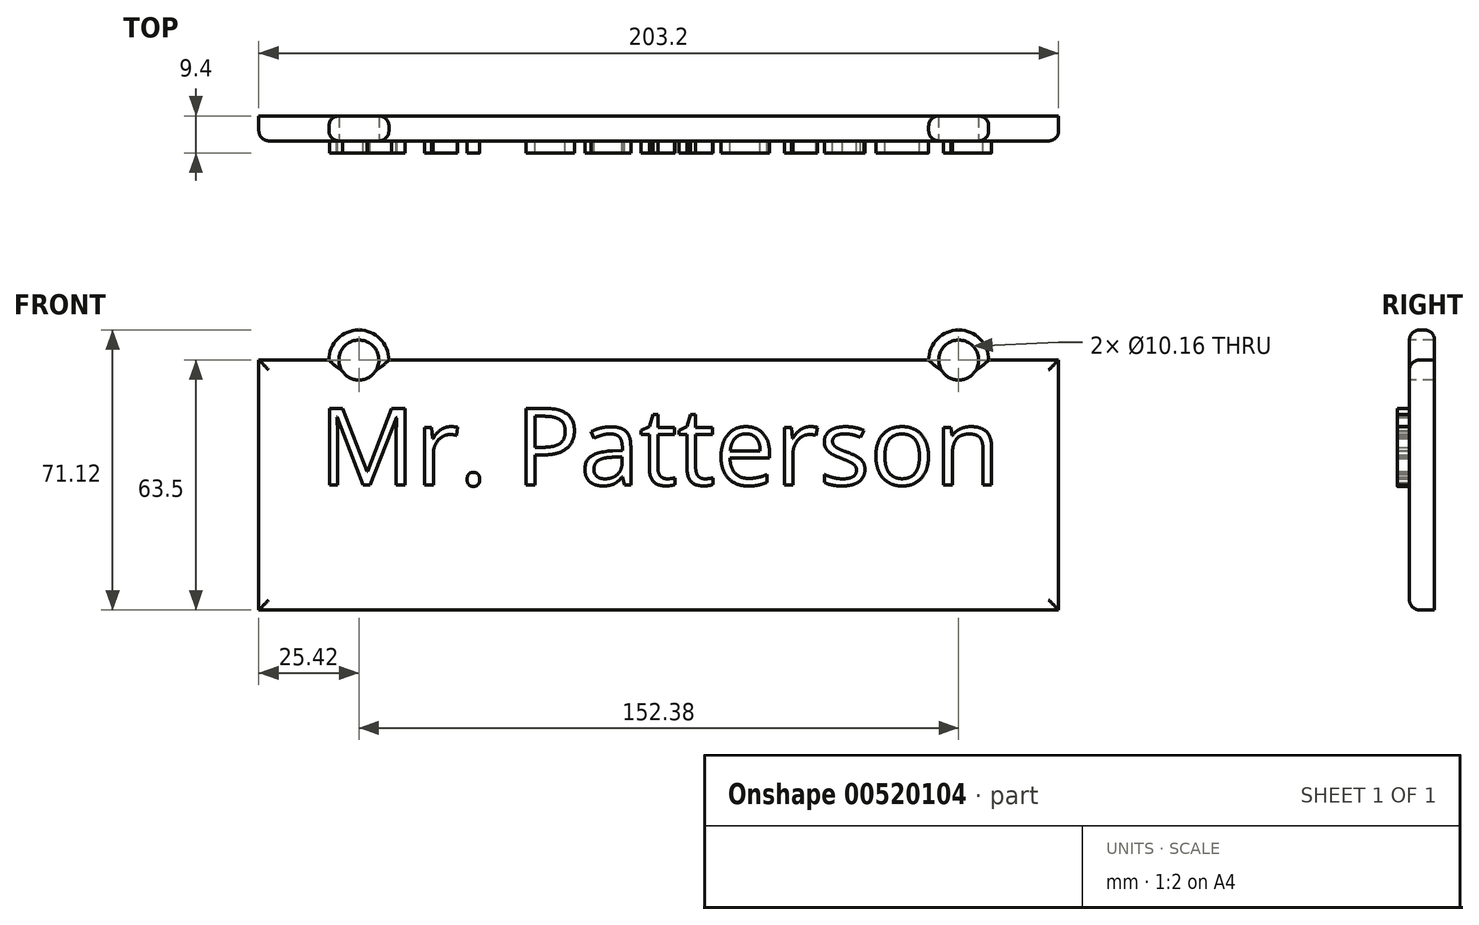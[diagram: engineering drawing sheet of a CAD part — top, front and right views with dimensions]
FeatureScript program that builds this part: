
annotation { "Feature Type Name" : "Feature", "Feature Type Description" : "" }
export const myFeature = defineFeature(function(context is Context, id is Id, definition is map)
    precondition{}
    {
        {
            var Q0;
            Q0=qCreatedBy(makeId("Front.planeOp"),FACE);
            var sketch = newSketch(context, id + "F0", { "sketchPlane" : qUnion([Q0])});
            skLineSegment(sketch, "E0.bottom", {"start": v(101.6, 31.75) * mm, "end": v(-101.6, 31.75) * mm});
            skLineSegment(sketch, "E0.top", {"start": v(101.6, -31.75) * mm, "end": v(-101.6, -31.75) * mm});
            skLineSegment(sketch, "E0.left", {"start": v(101.6, 31.75) * mm, "end": v(101.6, -31.75) * mm});
            skLineSegment(sketch, "E0.right", {"start": v(-101.6, 31.75) * mm, "end": v(-101.6, -31.75) * mm});
            skPoint(sketch, "E0.middle", {"position": v(0, 0) * mm});
            skSolve(sketch);
        }
        {
            var Q0;
            Q0=makeQuery(id+"F0.imprint","IMPRINT",FACE,{"disambiguationData":[TD([[makeQuery(id+"F0.imprint","IMPRINT",EDGE,{"derivedFrom":sQuery(id+"F0.wireOp",EDGE,"E0.bottom")}),1.0]])]});
            extrude(context, id + "F1", {"entities" : qUnion([Q0]), "depth" : 6.35 * mm, "offsetDistance" : 25.4 * mm});
        }
        {
            var Q0;
            Q0=makeQuery(id+"F1.opExtrude","CAP_FACE",FACE,{"disambiguationData":[OSD([sQuery(id+"F0.wireOp",EDGE,"E0.bottom"),sQuery(id+"F0.wireOp",EDGE,"E0.top"),sQuery(id+"F0.wireOp",EDGE,"E0.left"),sQuery(id+"F0.wireOp",EDGE,"E0.right")])],"isStart":false});
            var sketch = newSketch(context, id + "F2", { "sketchPlane" : qUnion([Q0])});
            skCircle(sketch, "E1", {"center": v(-76.18, 31.75) * mm, "radius": 7.62 * mm});
            skCircle(sketch, "E2", {"center": v(76.2, 31.75) * mm, "radius": 7.62 * mm});
            skSolve(sketch);
        }
        {
            var Q0;
            {var subQ0=sQuery(id+"F2.wireOp",EDGE,"E1");var subQ1=makeQuery(id+"F1.opExtrude","CAP_EDGE",EDGE,{"disambiguationData":[OSD([sQuery(id+"F0.wireOp",EDGE,"E0.bottom")])],"isStart":false});var subQ2=makeQuery(id+"F2.imprint","INTERSECT",VERTEX,{"disambiguationData":[OD(0.0)],"derivedFrom":[subQ1,subQ0]});Q0=makeQuery(id+"F2.imprint","IMPRINT",FACE,{"disambiguationData":[TD([[makeQuery(id+"F2.imprint","IMPRINT",EDGE,{"disambiguationData":[TD([[subQ2,1.0]])],"derivedFrom":subQ0}),1.0]])]});}
            var Q1;
            {var subQ0=sQuery(id+"F2.wireOp",EDGE,"E2");var subQ1=makeQuery(id+"F1.opExtrude","CAP_EDGE",EDGE,{"disambiguationData":[OSD([sQuery(id+"F0.wireOp",EDGE,"E0.bottom")])],"isStart":false});var subQ2=makeQuery(id+"F2.imprint","INTERSECT",VERTEX,{"disambiguationData":[OD(0.0)],"derivedFrom":[subQ1,subQ0]});Q1=makeQuery(id+"F2.imprint","IMPRINT",FACE,{"disambiguationData":[TD([[makeQuery(id+"F2.imprint","IMPRINT",EDGE,{"disambiguationData":[TD([[subQ2,-1.0]])],"derivedFrom":subQ0}),1.0]])]});}
            extrude(context, id + "F3", {"entities" : qUnion([Q0, Q1]), "operationType" : NewBodyOperationType.ADD, "depth" : -6.35 * mm, "offsetDistance" : 25.4 * mm});
        }
        {
            var Q0;
            {var subQ0=sQuery(id+"F0.wireOp",EDGE,"E0.bottom");Q0=makeQuery(id+"F3.boolean.opBoolean","MERGE",FACE,{"derivedFrom":[makeQuery(id+"F1.opExtrude","CAP_FACE",FACE,{"disambiguationData":[OSD([subQ0,sQuery(id+"F0.wireOp",EDGE,"E0.top"),sQuery(id+"F0.wireOp",EDGE,"E0.left"),sQuery(id+"F0.wireOp",EDGE,"E0.right")])],"isStart":false}),makeQuery(id+"F3.opExtrude","CAP_FACE",FACE,{"disambiguationData":[OSD([subQ0,sQuery(id+"F2.wireOp",EDGE,"E1")])],"isStart":true}),makeQuery(id+"F3.opExtrude","CAP_FACE",FACE,{"disambiguationData":[OSD([subQ0,sQuery(id+"F2.wireOp",EDGE,"E2")])],"isStart":true})]});}
            var sketch = newSketch(context, id + "F4", { "sketchPlane" : qUnion([Q0])});
            skCircle(sketch, "E3", {"center": v(-76.18, 31.75) * mm, "radius": 5.08 * mm});
            skCircle(sketch, "E4", {"center": v(76.2, 31.75) * mm, "radius": 5.08 * mm});
            skSolve(sketch);
        }
        {
            var Q0;
            Q0=makeQuery(id+"F4.imprint","IMPRINT",FACE,{"disambiguationData":[TD([[makeQuery(id+"F4.imprint","IMPRINT",EDGE,{"derivedFrom":sQuery(id+"F4.wireOp",EDGE,"E3")}),1.0]])]});
            var Q1;
            Q1=makeQuery(id+"F4.imprint","IMPRINT",FACE,{"disambiguationData":[TD([[makeQuery(id+"F4.imprint","IMPRINT",EDGE,{"derivedFrom":sQuery(id+"F4.wireOp",EDGE,"E4")}),1.0]])]});
            extrude(context, id + "F5", {"entities" : qUnion([Q0, Q1]), "operationType" : NewBodyOperationType.REMOVE, "oppositeDirection" : true, "depth" : 6.35 * mm, "offsetDistance" : 25.4 * mm});
        }
        {
            var Q0;
            Q0=makeQuery(id+"F1.opExtrude","CAP_EDGE",EDGE,{"disambiguationData":[OSD([sQuery(id+"F0.wireOp",EDGE,"E0.top")])],"isStart":false});
            var Q1;
            Q1=makeQuery(id+"F1.opExtrude","CAP_EDGE",EDGE,{"disambiguationData":[OSD([sQuery(id+"F0.wireOp",EDGE,"E0.right")])],"isStart":false});
            var Q2;
            {var subQ0=sQuery(id+"F2.wireOp",EDGE,"E1");var subQ1=sQuery(id+"F0.wireOp",EDGE,"E0.right");var subQ2=sQuery(id+"F0.wireOp",EDGE,"E0.bottom");Q2=makeQuery(id+"F3.boolean.opBoolean","SPLIT",EDGE,{"disambiguationData":[TD([makeQuery(id+"F1.opExtrude","SWEPT_FACE",FACE,{"disambiguationData":[OSD([subQ2])]}),makeQuery(id+"F1.opExtrude","CAP_FACE",FACE,{"disambiguationData":[OSD([subQ2,sQuery(id+"F0.wireOp",EDGE,"E0.top"),sQuery(id+"F0.wireOp",EDGE,"E0.left"),subQ1])],"isStart":false}),makeQuery(id+"F1.opExtrude","SWEPT_FACE",FACE,{"disambiguationData":[OSD([subQ1])]}),makeQuery(id+"F3.opExtrude","SWEPT_FACE",FACE,{"disambiguationData":[OSD([subQ0])]}),makeQuery(id+"F3.opExtrude","CAP_FACE",FACE,{"disambiguationData":[OSD([subQ2,subQ0])],"isStart":true}),makeQuery(id+"F3.opExtrude","CAP_FACE",FACE,{"disambiguationData":[OSD([subQ2,sQuery(id+"F2.wireOp",EDGE,"E2")])],"isStart":true})])],"derivedFrom":makeQuery(id+"F1.opExtrude","CAP_EDGE",EDGE,{"disambiguationData":[OSD([subQ2])],"isStart":false})});}
            var Q3;
            Q3=makeQuery(id+"F3.opExtrude","CAP_EDGE",EDGE,{"disambiguationData":[OSD([sQuery(id+"F2.wireOp",EDGE,"E1")])],"isStart":true});
            var Q4;
            {var subQ0=sQuery(id+"F2.wireOp",EDGE,"E1");var subQ1=sQuery(id+"F0.wireOp",EDGE,"E0.bottom");var subQ2=sQuery(id+"F2.wireOp",EDGE,"E2");Q4=makeQuery(id+"F3.boolean.opBoolean","SPLIT",EDGE,{"disambiguationData":[TD([makeQuery(id+"F1.opExtrude","SWEPT_FACE",FACE,{"disambiguationData":[OSD([subQ1])]}),makeQuery(id+"F1.opExtrude","CAP_FACE",FACE,{"disambiguationData":[OSD([subQ1,sQuery(id+"F0.wireOp",EDGE,"E0.top"),sQuery(id+"F0.wireOp",EDGE,"E0.left"),sQuery(id+"F0.wireOp",EDGE,"E0.right")])],"isStart":false}),makeQuery(id+"F3.opExtrude","SWEPT_FACE",FACE,{"disambiguationData":[OSD([subQ0])]}),makeQuery(id+"F3.opExtrude","CAP_FACE",FACE,{"disambiguationData":[OSD([subQ1,subQ0])],"isStart":true}),makeQuery(id+"F3.opExtrude","SWEPT_FACE",FACE,{"disambiguationData":[OSD([subQ2])]}),makeQuery(id+"F3.opExtrude","CAP_FACE",FACE,{"disambiguationData":[OSD([subQ1,subQ2])],"isStart":true})])],"derivedFrom":makeQuery(id+"F1.opExtrude","CAP_EDGE",EDGE,{"disambiguationData":[OSD([subQ1])],"isStart":false})});}
            var Q5;
            Q5=makeQuery(id+"F3.opExtrude","CAP_EDGE",EDGE,{"disambiguationData":[OSD([sQuery(id+"F2.wireOp",EDGE,"E2")])],"isStart":true});
            var Q6;
            {var subQ0=sQuery(id+"F0.wireOp",EDGE,"E0.bottom");var subQ1=sQuery(id+"F0.wireOp",EDGE,"E0.left");var subQ2=sQuery(id+"F2.wireOp",EDGE,"E2");Q6=makeQuery(id+"F3.boolean.opBoolean","SPLIT",EDGE,{"disambiguationData":[TD([makeQuery(id+"F1.opExtrude","SWEPT_FACE",FACE,{"disambiguationData":[OSD([subQ0])]}),makeQuery(id+"F1.opExtrude","CAP_FACE",FACE,{"disambiguationData":[OSD([subQ0,sQuery(id+"F0.wireOp",EDGE,"E0.top"),subQ1,sQuery(id+"F0.wireOp",EDGE,"E0.right")])],"isStart":false}),makeQuery(id+"F1.opExtrude","SWEPT_FACE",FACE,{"disambiguationData":[OSD([subQ1])]}),makeQuery(id+"F3.opExtrude","CAP_FACE",FACE,{"disambiguationData":[OSD([subQ0,sQuery(id+"F2.wireOp",EDGE,"E1")])],"isStart":true}),makeQuery(id+"F3.opExtrude","SWEPT_FACE",FACE,{"disambiguationData":[OSD([subQ2])]}),makeQuery(id+"F3.opExtrude","CAP_FACE",FACE,{"disambiguationData":[OSD([subQ0,subQ2])],"isStart":true})])],"derivedFrom":makeQuery(id+"F1.opExtrude","CAP_EDGE",EDGE,{"disambiguationData":[OSD([subQ0])],"isStart":false})});}
            var Q7;
            Q7=makeQuery(id+"F1.opExtrude","CAP_EDGE",EDGE,{"disambiguationData":[OSD([sQuery(id+"F0.wireOp",EDGE,"E0.left")])],"isStart":false});
            var Q8;
            Q8=makeQuery(id+"F5.boolean.opBoolean","COPY",EDGE,{"derivedFrom":makeQuery(id+"F5.opExtrude","CAP_EDGE",EDGE,{"disambiguationData":[OSD([sQuery(id+"F4.wireOp",EDGE,"E3")])],"isStart":true})});
            var Q9;
            Q9=makeQuery(id+"F5.boolean.opBoolean","COPY",EDGE,{"derivedFrom":makeQuery(id+"F5.opExtrude","CAP_EDGE",EDGE,{"disambiguationData":[OSD([sQuery(id+"F4.wireOp",EDGE,"E4")])],"isStart":true})});
            var Q10;
            Q10=makeQuery(id+"F3.opExtrude","CAP_EDGE",EDGE,{"disambiguationData":[OSD([sQuery(id+"F2.wireOp",EDGE,"E2")])],"isStart":false});
            var Q11;
            Q11=makeQuery(id+"F3.opExtrude","CAP_EDGE",EDGE,{"disambiguationData":[OSD([sQuery(id+"F2.wireOp",EDGE,"E1")])],"isStart":false});
            fillet(context, id + "F6", {"entities" : qUnion([Q0, Q1, Q2, Q3, Q4, Q5, Q6, Q7, Q8, Q9, Q10, Q11]), "radius" : 2.54 * mm, "tangentPropagation" : true, "allowEdgeOverflow" : false});
        }
        {
            var Q0;
            {var subQ0=sQuery(id+"F0.wireOp",EDGE,"E0.bottom");Q0=makeQuery(id+"F3.boolean.opBoolean","MERGE",FACE,{"derivedFrom":[makeQuery(id+"F1.opExtrude","CAP_FACE",FACE,{"disambiguationData":[OSD([subQ0,sQuery(id+"F0.wireOp",EDGE,"E0.top"),sQuery(id+"F0.wireOp",EDGE,"E0.left"),sQuery(id+"F0.wireOp",EDGE,"E0.right")])],"isStart":false}),makeQuery(id+"F3.opExtrude","CAP_FACE",FACE,{"disambiguationData":[OSD([subQ0,sQuery(id+"F2.wireOp",EDGE,"E1")])],"isStart":true}),makeQuery(id+"F3.opExtrude","CAP_FACE",FACE,{"disambiguationData":[OSD([subQ0,sQuery(id+"F2.wireOp",EDGE,"E2")])],"isStart":true})]});}
            var sketch = newSketch(context, id + "F7", { "sketchPlane" : qUnion([Q0])});
            skText(sketch, "E5", { "text": "Mr. Patterson", "fontName": "OpenSans-Regular.ttf"});
            const initialGuessF7  = {"E5": [-0.08636, 0, 1, 0, 0.01958]};
            skSetInitialGuess(sketch, initialGuessF7);
            skSolve(sketch);
        }
        {
            var Q0;
            Q0 = qSketchRegion(id + "F7", true);
            extrude(context, id + "F8", {"entities" : qUnion([Q0]), "operationType" : NewBodyOperationType.ADD, "depth" : 3.05 * mm, "offsetDistance" : 25.4 * mm});
        }
    });
